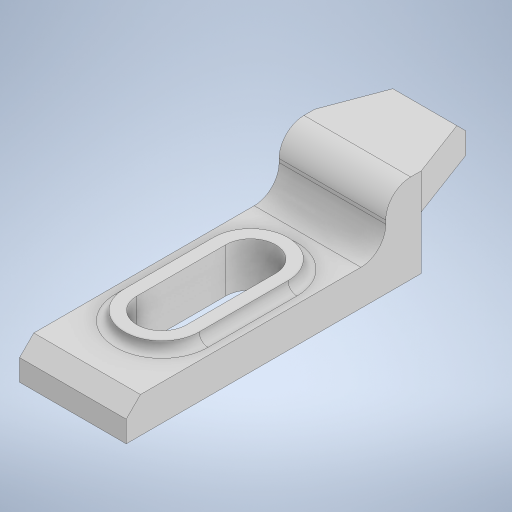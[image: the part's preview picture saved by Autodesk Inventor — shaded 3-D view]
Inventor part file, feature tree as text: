
AUTODESK INVENTOR PART (.ipt)
format: ipt  version: 2023 (Build 270158000, 158)  size: 292,352 bytes
history: native  units: mm
features: extrude x4, fillet x2, sketch x1, chamfer x1
ambient origin geometry x8: Origin, YZ Plane, XZ Plane, XY Plane, X Axis, Y Axis, Z Axis, Center Point
bodies: Solido1 (feature_tree)
feature tree (8):
  sketch  "Schizzo1"
  extrude  "Estrusione1"  Depth=83.0mm
  extrude  "Estrusione2"  Depth=20.0mm
  extrude  "Estrusione3"  Depth=30.0mm
  extrude  "Estrusione4"  Depth=30.0mm
  fillet  "Raccordo1"  Radius=25.0mm
  fillet  "Raccordo2"  Radius=25.0mm
  chamfer  "Smusso1"  Distance=7.5mm
